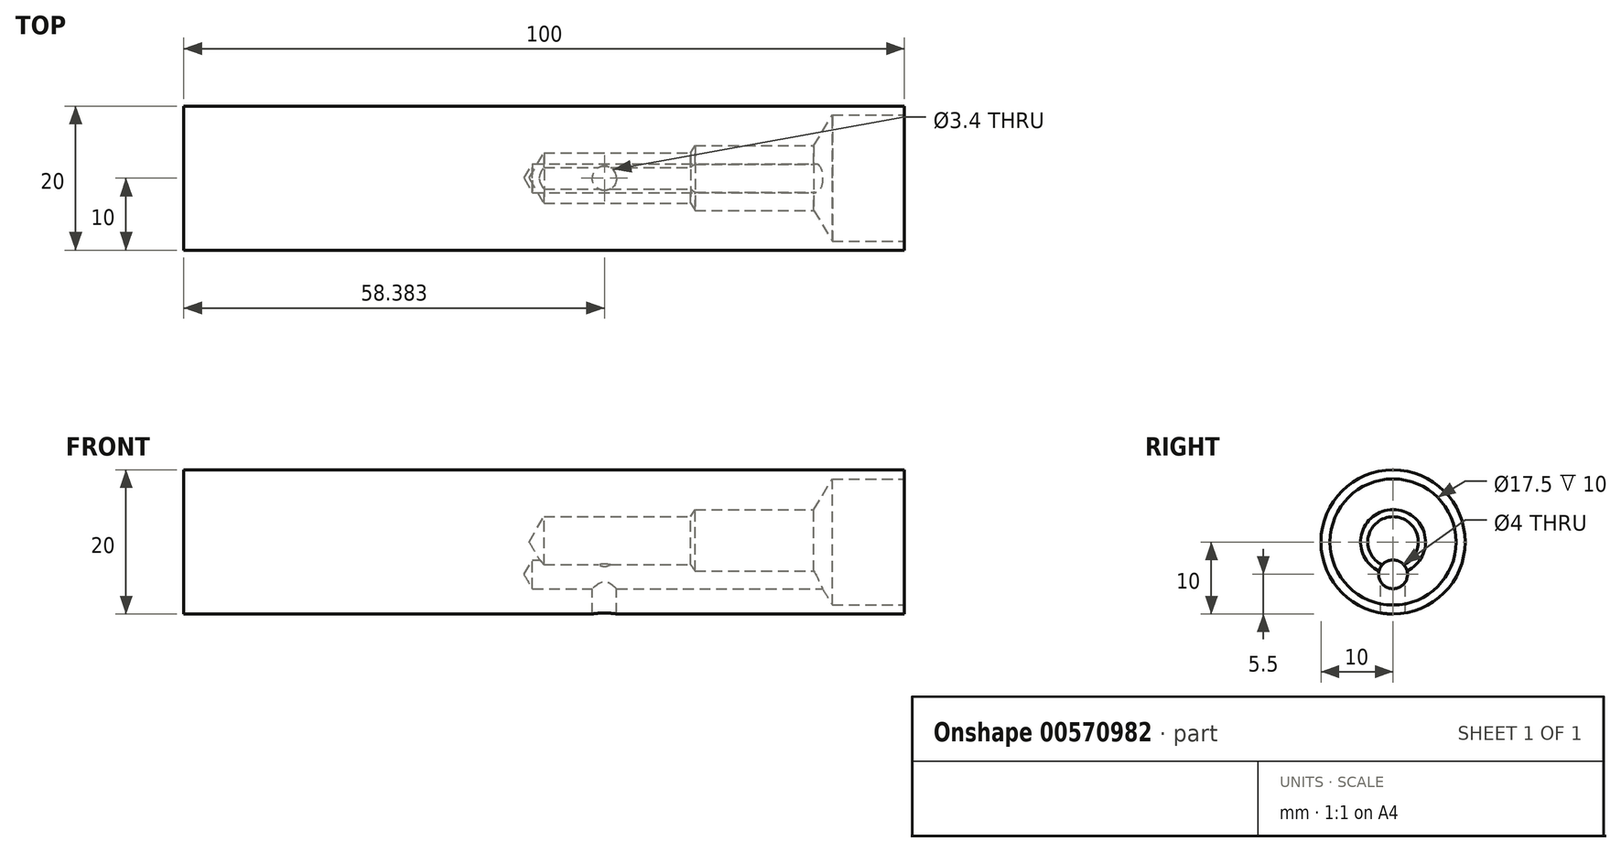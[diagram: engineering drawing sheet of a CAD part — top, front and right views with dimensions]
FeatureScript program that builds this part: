
annotation { "Feature Type Name" : "Feature", "Feature Type Description" : "" }
export const myFeature = defineFeature(function(context is Context, id is Id, definition is map)
    precondition{}
    {
        {
            var Q0;
            Q0=qCreatedBy(makeId("Right.planeOp"),FACE);
            var sketch = newSketch(context, id + "F0", { "sketchPlane" : qUnion([Q0])});
            skCircle(sketch, "E0", {"center": v(0, 0) * mm, "radius": 10 * mm});
            skSolve(sketch);
        }
        {
            var Q0;
            Q0 = qSketchRegion(id + "F0", true);
            extrude(context, id + "F1", {"entities" : qUnion([Q0]), "depth" : 100 * mm, "offsetDistance" : 25 * mm});
        }
        {
            var Q0;
            Q0=makeQuery(id+"F1.opExtrude","CAP_FACE",FACE,{"disambiguationData":[OSD([sQuery(id+"F0.wireOp",EDGE,"E0")])],"isStart":false});
            var sketch = newSketch(context, id + "F2", { "sketchPlane" : qUnion([Q0])});
            skPoint(sketch, "E1", {"position": v(0, 0) * mm});
            skSolve(sketch);
        }
        {
            var Q0;
            Q0=sQuery(id+"F2.wireOp",VERTEX,"E1");
            var Q1;
            Q1=makeQuery(id+"F1.opExtrude","SWEPT_BODY",BODY,{"disambiguationData":[OSD([sQuery(id+"F0.wireOp",EDGE,"E0")])]});
            hole(context, id + "F3", {"style" : HoleStyle.SIMPLE, "endStyle" : HoleEndStyle.BLIND, "holeDiameter" : 17.5 * mm, "holeDepth" : 10 * mm, "isTappedThrough" : true, "tappedDepth" : 12 * mm, "tapClearance" : 3, "locations" : qUnion([Q0]), "scope" : qUnion([Q1])});
        }
        {
            var Q0;
            Q0=makeQuery(id+"F1.opExtrude","CAP_FACE",FACE,{"disambiguationData":[OSD([sQuery(id+"F0.wireOp",EDGE,"E0")])],"isStart":false});
            var sketch = newSketch(context, id + "F4", { "sketchPlane" : qUnion([Q0])});
            skPoint(sketch, "E2", {"position": v(0, 0) * mm});
            skSolve(sketch);
        }
        {
            var Q0;
            Q0=sQuery(id+"F4.wireOp",VERTEX,"E2");
            var Q1;
            Q1=makeQuery(id+"F1.opExtrude","SWEPT_BODY",BODY,{"disambiguationData":[OSD([sQuery(id+"F0.wireOp",EDGE,"E0")])]});
            hole(context, id + "F5", {"style" : HoleStyle.SIMPLE, "endStyle" : HoleEndStyle.BLIND, "holeDiameter" : 9 * mm, "holeDepth" : 16.5 * mm, "isTappedThrough" : true, "tappedDepth" : 12 * mm, "tapClearance" : 3, "locations" : qUnion([Q0]), "scope" : qUnion([Q1])});
        }
        {
            var Q0;
            Q0=sQuery(id+"F4.wireOp",VERTEX,"E2");
            var Q1;
            Q1=makeQuery(id+"F1.opExtrude","SWEPT_BODY",BODY,{"disambiguationData":[OSD([sQuery(id+"F0.wireOp",EDGE,"E0")])]});
            hole(context, id + "F6", {"style" : HoleStyle.SIMPLE, "endStyle" : HoleEndStyle.BLIND, "holeDiameter" : 7 * mm, "holeDepth" : 50 * mm, "isTappedThrough" : true, "tappedDepth" : 12 * mm, "tapClearance" : 3, "startFromSketch" : true, "locations" : qUnion([Q0]), "scope" : qUnion([Q1])});
        }
        {
            var Q0;
            Q0=qCreatedBy(makeId("Top.planeOp"),FACE);
            var sketch = newSketch(context, id + "F7", { "sketchPlane" : qUnion([Q0])});
            skPoint(sketch, "E3", {"position": v(58.38, 0) * mm});
            skSolve(sketch);
        }
        {
            var Q0;
            Q0=sQuery(id+"F7.wireOp",VERTEX,"E3");
            var Q1;
            Q1=makeQuery(id+"F1.opExtrude","SWEPT_BODY",BODY,{"disambiguationData":[OSD([sQuery(id+"F0.wireOp",EDGE,"E0")])]});
            hole(context, id + "F8", {"style" : HoleStyle.SIMPLE, "endStyle" : HoleEndStyle.BLIND, "holeDiameter" : 3.4 * mm, "holeDepth" : 50 * mm, "isTappedThrough" : true, "tappedDepth" : 12 * mm, "tapClearance" : 3, "locations" : qUnion([Q0]), "scope" : qUnion([Q1])});
        }
        {
            var Q0;
            Q0=makeQuery(id+"F4.imprint","IMPRINT",FACE,{"disambiguationData":[TD([[makeQuery(id+"F4.imprint","IMPRINT",EDGE,{"derivedFrom":makeQuery(id+"F1.opExtrude","CAP_EDGE",EDGE,{"disambiguationData":[OSD([sQuery(id+"F0.wireOp",EDGE,"E0")])],"isStart":false})}),1.0]])]});
            var sketch = newSketch(context, id + "F9", { "sketchPlane" : qUnion([Q0])});
            skPoint(sketch, "E4", {"position": v(0, -4.5) * mm});
            skSolve(sketch);
        }
        {
            var Q0;
            Q0=sQuery(id+"F9.wireOp",VERTEX,"E4");
            var Q1;
            Q1=makeQuery(id+"F1.opExtrude","SWEPT_BODY",BODY,{"disambiguationData":[OSD([sQuery(id+"F0.wireOp",EDGE,"E0")])]});
            hole(context, id + "F10", {"style" : HoleStyle.SIMPLE, "endStyle" : HoleEndStyle.BLIND, "holeDiameter" : 4 * mm, "holeDepth" : 1 * mm, "isTappedThrough" : true, "tappedDepth" : 12 * mm, "tapClearance" : 3, "locations" : qUnion([Q0]), "scope" : qUnion([Q1])});
        }
    });
